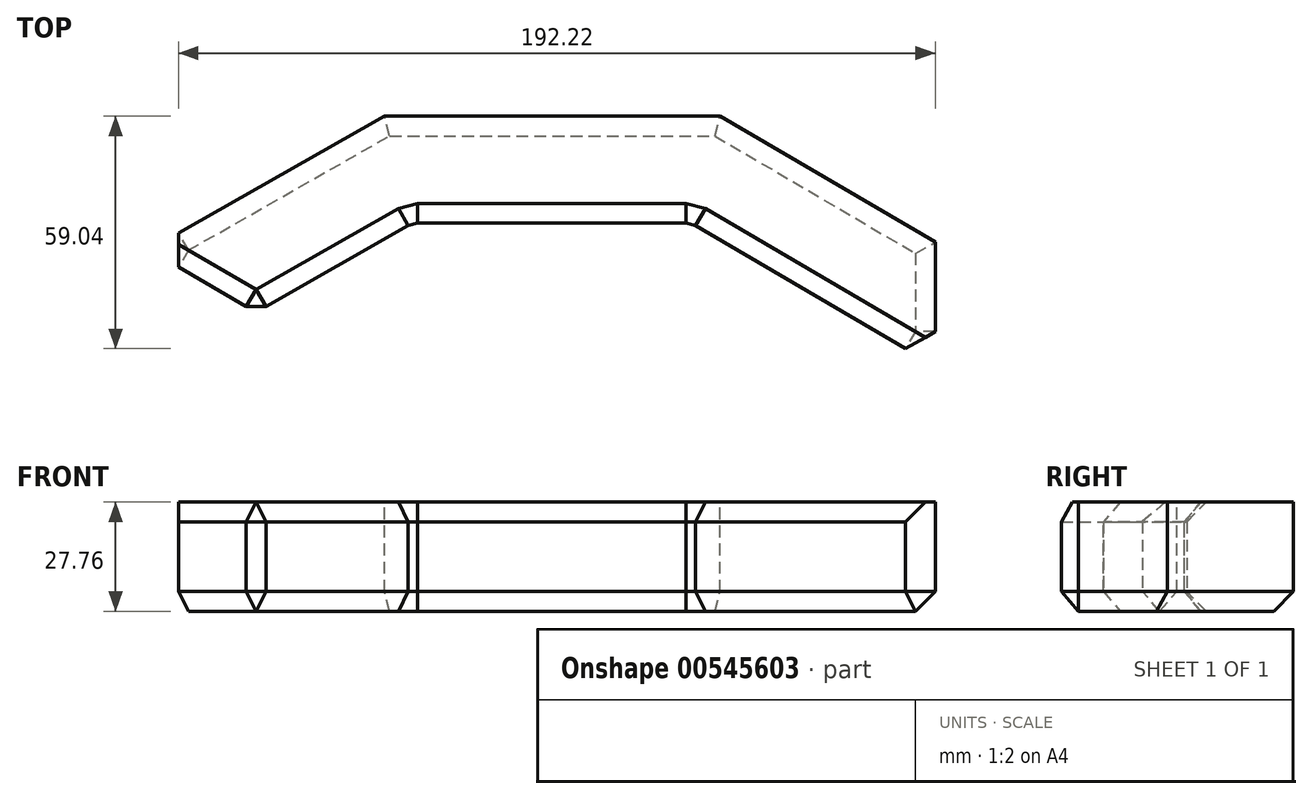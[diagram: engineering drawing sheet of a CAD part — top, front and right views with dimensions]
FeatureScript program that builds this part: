
annotation { "Feature Type Name" : "Feature", "Feature Type Description" : "" }
export const myFeature = defineFeature(function(context is Context, id is Id, definition is map)
    precondition{}
    {
        {
            var Q0;
            Q0=qCreatedBy(makeId("Right.planeOp"),FACE);
            var sketch = newSketch(context, id + "F0", { "sketchPlane" : qUnion([Q0])});
            skLineSegment(sketch, "E0.bottom", {"start": v(-17.56, 51.84) * mm, "end": v(13.88, 51.84) * mm});
            skLineSegment(sketch, "E0.top", {"start": v(-17.56, 24.08) * mm, "end": v(13.88, 24.08) * mm});
            skLineSegment(sketch, "E0.left", {"start": v(-17.56, 51.84) * mm, "end": v(-17.56, 24.08) * mm});
            skLineSegment(sketch, "E0.right", {"start": v(13.88, 51.84) * mm, "end": v(13.88, 24.08) * mm});
            skSolve(sketch);
        }
        {
            var Q0;
            Q0=qCreatedBy(makeId("Top.planeOp"),FACE);
            var sketch = newSketch(context, id + "F1", { "sketchPlane" : qUnion([Q0])});
            skLineSegment(sketch, "E1", {"start": v(0, 13.81) * mm, "end": v(-54.67, 45.82) * mm});
            skLineSegment(sketch, "E2", {"start": v(-54.67, 45.82) * mm, "end": v(-139.94, 45.82) * mm});
            skLineSegment(sketch, "E3", {"start": v(-139.94, 45.82) * mm, "end": v(-199.7, 11.83) * mm});
            skSolve(sketch);
        }
        {
            var Q0;
            Q0 = qSketchRegion(id + "F0", true);
            var Q1;
            Q1 = qConstructionFilter(qBodyType(qCreatedBy(id + "F1" ,EDGE), BodyType.WIRE), ConstructionObject.NO);
            sweep(context, id + "F2", {"profiles" : qUnion([Q0]), "path" : qUnion([Q1])});
        }
        {
            var Q0;
            Q0=makeQuery(id+"F2.opSweep","SWEPT_FACE",FACE,{"disambiguationData":[OSD([sQuery(id+"F0.wireOp",EDGE,"E0.left"),sQuery(id+"F1.wireOp",EDGE,"E2")])]});
            var Q1;
            Q1=makeQuery(id+"F2.opSweep","SWEPT_FACE",FACE,{"disambiguationData":[OSD([sQuery(id+"F0.wireOp",EDGE,"E0.left"),sQuery(id+"F1.wireOp",EDGE,"E3")])]});
            var Q2;
            Q2=makeQuery(id+"F2.opSweep","CAP_FACE",FACE,{"disambiguationData":[OSD([sQuery(id+"F0.wireOp",EDGE,"E0.bottom"),sQuery(id+"F0.wireOp",EDGE,"E0.top"),sQuery(id+"F0.wireOp",EDGE,"E0.left"),sQuery(id+"F0.wireOp",EDGE,"E0.right"),sQuery(id+"F1.wireOp",VERTEX,"E3.end")])],"isStart":false});
            var Q3;
            Q3=makeQuery(id+"F2.opSweep","SWEPT_EDGE",EDGE,{"disambiguationData":[OSD([sQuery(id+"F0.wireOp",EDGE,"E0.top"),sQuery(id+"F0.wireOp",EDGE,"E0.right"),sQuery(id+"F1.wireOp",EDGE,"E2")])]});
            var Q4;
            Q4=makeQuery(id+"F2.opSweep","SWEPT_EDGE",EDGE,{"disambiguationData":[OSD([sQuery(id+"F0.wireOp",EDGE,"E0.top"),sQuery(id+"F0.wireOp",EDGE,"E0.right"),sQuery(id+"F1.wireOp",EDGE,"E3")])]});
            var Q5;
            Q5=makeQuery(id+"F2.opSweep","SWEPT_EDGE",EDGE,{"disambiguationData":[OSD([sQuery(id+"F0.wireOp",EDGE,"E0.top"),sQuery(id+"F0.wireOp",EDGE,"E0.right"),sQuery(id+"F1.wireOp",EDGE,"E1")])]});
            var Q6;
            Q6=makeQuery(id+"F2.opSweep","SWEPT_FACE",FACE,{"disambiguationData":[OSD([sQuery(id+"F0.wireOp",EDGE,"E0.top"),sQuery(id+"F1.wireOp",EDGE,"E1")])]});
            var Q7;
            Q7=makeQuery(id+"F2.opSweep","CAP_EDGE",EDGE,{"disambiguationData":[OSD([sQuery(id+"F0.wireOp",EDGE,"E0.left"),sQuery(id+"F1.wireOp",VERTEX,"E1.start")])],"isStart":true});
            chamfer(context, id + "F3", {"entities" : qUnion([Q0, Q1, Q2, Q3, Q4, Q5, Q6, Q7]), "width" : 5 * mm, "tangentPropagation" : true});
        }
    });
